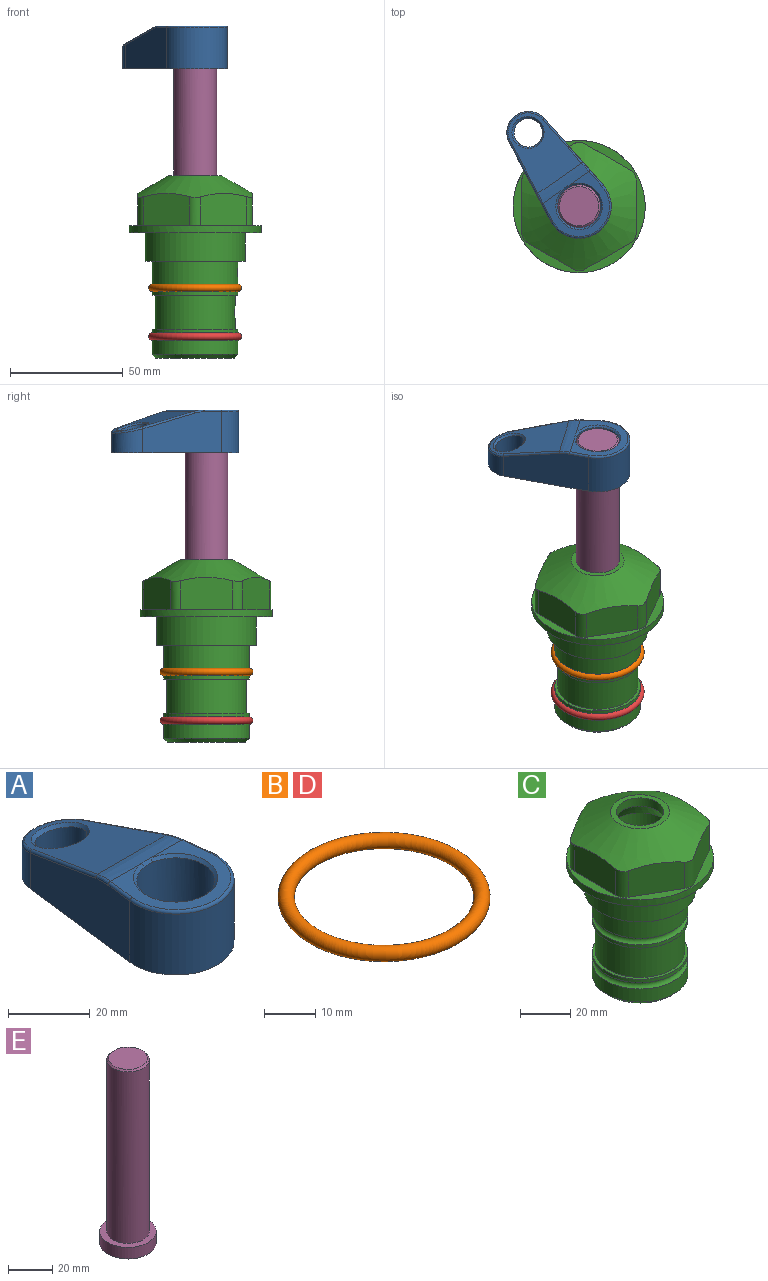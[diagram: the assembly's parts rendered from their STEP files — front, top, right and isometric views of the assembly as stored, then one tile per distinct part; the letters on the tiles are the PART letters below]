
ASSEMBLY  parts=5 mates=4
PART A: 31 faces, bbox 31.7x65.5x19.8 mm
  f0: plane 39.12x18.26mm, normal (0.99,0.12,0), area 612.2mm2, adj f1,f4,f7,f11,f13,f15
  f1: cylinder r=9.53mm len=18.91mm, axis (0,0,-1), area 296.1mm2, adj f0,f2,f7,f17
  f2: plane 39.12x18.26mm, normal (-0.99,0.12,0), area 612.2mm2, adj f1,f4,f7,f12,f14,f16
  f3: cylinder r=6.35mm len=12.7mm, axis (0,0,-1), area 362.4mm2, adj f7,f18
  f4: cylinder r=14.29mm len=28.58mm, axis (0,0,-1), area 882.2mm2, adj f0,f2,f7,f10
  f5: cylinder r=9.53mm len=19.05mm, axis (0,0,-1), area 1092.6mm2, adj f7,f19,f20
  f6: plane 26.99x23.69mm, normal (0,0,1), area 216.2mm2, adj f9,f10,f11,f12,f19
  f7: plane 63.5x28.58mm, normal (0,0,-1), area 661.8mm2, adj f0,f1,f2,f3,f4,f5,f22,f23
  f8: plane 33.52x23.6mm, normal (0,0.26,0.97), area 486mm2, adj f9,f15,f16,f17,f18
  f9: cylinder r=19.05mm len=24.72mm, axis (1,0,0), area 120.4mm2, adj f6,f8,f13,f14,f20
  f10: torus R=13.49mm, axis (0,0,1), area 59mm2, adj f4,f6,f11,f12
  f11: cylinder r=0.79mm len=8.67mm, axis (0.12,-0.99,0), area 10.8mm2, adj f0,f6,f10,f13
  f12: cylinder r=0.79mm len=8.67mm, axis (0.12,0.99,0), area 10.8mm2, adj f2,f6,f10,f14
  f13: bspline ~4.95x1.42mm, area 6.1mm2, adj f0,f9,f11,f15
  f14: bspline ~4.95x1.42mm, area 6.1mm2, adj f2,f9,f12,f16
  f15: cylinder r=0.79mm len=25.95mm, axis (0.12,-0.96,0.26), area 32.9mm2, adj f0,f8,f13,f17
  f16: cylinder r=0.79mm len=25.95mm, axis (0.12,0.96,-0.26), area 32.9mm2, adj f2,f8,f14,f17
  f17: bspline ~18.91x8.38mm, area 30mm2, adj f1,f8,f15,f16
  f18: bspline ~14.29x14.29mm, area 48.3mm2, adj f3,f8
  f19: cone r=9.53mm half-angle=45deg, axis (0,0,1), area 66.5mm2, adj f5,f6,f20
  f20: bspline ~3.22x0.96mm, area 3.5mm2, adj f5,f9,f19
  f21: plane 2.75x2.72mm, normal (0,0,-1), area 2.9mm2, adj f23,f25,f28
  f22: plane 23.05x15.88mm, normal (-0.99,-0.12,0), area 323.6mm2, adj f7,f25,f26,f27,f28,f29
  f23: plane 23.05x15.88mm, normal (0.99,-0.12,0), area 323.6mm2, adj f7,f21,f25,f27,f28,f30
  f24: cylinder r=9.53mm len=10.69mm, axis (0,0,-1), area 114.7mm2, adj f7,f27,f29,f30
  f25: cylinder r=12.7mm len=20.59mm, axis (0,0,-1), area 381.1mm2, adj f7,f21,f22,f23,f26,f28
  f26: plane 2.75x2.72mm, normal (0,0,-1), area 2.9mm2, adj f22,f25,f28
  f27: plane 19.72x18.37mm, normal (0,-0.26,-0.97), area 291.8mm2, adj f22,f23,f24,f28,f29,f30
  f28: cylinder r=15.88mm len=19.92mm, axis (1,0,0), area 54.8mm2, adj f21,f22,f23,f25,f26,f27
  f29: cylinder r=1.59mm len=11mm, axis (0,0,-1), area 34.7mm2, adj f7,f22,f24,f27
  f30: cylinder r=1.59mm len=11mm, axis (0,0,-1), area 34.7mm2, adj f7,f23,f24,f27
PART B: 1 faces, bbox 44.7x44.7x3.2 mm
  f0: torus R=19.05mm, axis (0,0,1), area 1193.9mm2
PART C: 36 faces, bbox 58.7x58.7x81 mm
  f0: cylinder r=17.78mm len=35.56mm, axis (0,0,1), area 1670.8mm2, adj f23,f24,f31
  f1: cylinder r=19.05mm len=38.1mm, axis (0,0,1), area 1191.9mm2, adj f26,f27,f30
  f2: plane 58.66x58.66mm, normal (0,0,-1), area 1150.6mm2, adj f3,f28
  f3: cylinder r=29.33mm len=58.66mm, axis (0,0,-1), area 585.1mm2, adj f2,f4
  f4: plane 58.66x58.66mm, normal (0,0,1), area 475.9mm2, adj f3,f5,f6,f7,f8,f9,f10,f11
  f5: plane 20.32x14.34mm, normal (-0.5,0.87,0), area 324.4mm2, adj f4,f15,f16,f17
  f6: plane 20.32x14.34mm, normal (0.5,0.87,0), area 324.4mm2, adj f4,f14,f15,f17
  f7: plane 23.48x14.34mm, normal (1,0,0), area 324.4mm2, adj f4,f13,f14,f17
  f8: plane 20.32x14.34mm, normal (0.5,-0.87,0), area 324.4mm2, adj f4,f12,f13,f17
  f9: plane 20.32x14.34mm, normal (-0.5,-0.87,0), area 324.4mm2, adj f4,f11,f12,f17
  f10: plane 23.48x14.34mm, normal (-1,0,0), area 324.4mm2, adj f4,f11,f16,f17
  f11: cylinder r=5.08mm len=12.85mm, axis (0,0,-1), area 67.2mm2, adj f4,f9,f10,f17
  f12: cylinder r=5.08mm len=12.85mm, axis (0,0,-1), area 67.2mm2, adj f4,f8,f9,f17
  f13: cylinder r=5.08mm len=12.85mm, axis (0,0,-1), area 67.2mm2, adj f4,f7,f8,f17
  f14: cylinder r=5.08mm len=12.85mm, axis (0,0,-1), area 67.2mm2, adj f4,f6,f7,f17
  f15: cylinder r=5.08mm len=12.85mm, axis (0,0,-1), area 67.2mm2, adj f4,f5,f6,f17
  f16: cylinder r=5.08mm len=12.85mm, axis (0,0,-1), area 67.2mm2, adj f4,f5,f10,f17
  f17: cone r=11.73mm half-angle=60deg, axis (0,0,-1), area 2071.8mm2, adj f5,f6,f7,f8,f9,f10,f11,f12
  f18: plane 23.46x23.46mm, normal (0,0,1), area 147.4mm2, adj f17,f35
  f19: plane 34.93x34.93mm, normal (0,0,-1), area 958mm2, adj f29
  f20: cylinder r=19.05mm len=38.1mm, axis (0,0,1), area 760.1mm2, adj f21,f29
  f21: torus R=19.05mm, axis (0,0,1), area 565.3mm2, adj f20,f22
  f22: cylinder r=19.05mm len=38.1mm, axis (0,0,1), area 190mm2, adj f21,f23
  f23: plane 38.1x38.1mm, normal (0,0,1), area 146.9mm2, adj f0,f22
  f24: plane 38.1x38.1mm, normal (0,0,-1), area 146.9mm2, adj f0,f25
  f25: cylinder r=19.05mm len=38.1mm, axis (0,0,1), area 190mm2, adj f24,f26
  f26: torus R=19.05mm, axis (0,0,1), area 565.3mm2, adj f1,f25
  f27: plane 44.45x44.45mm, normal (0,0,-1), area 411.7mm2, adj f1,f28
  f28: cylinder r=22.23mm len=44.45mm, axis (0,0,1), area 1773.5mm2, adj f2,f27
  f29: cone r=19.05mm half-angle=45deg, axis (0,0,1), area 257.5mm2, adj f19,f20
  f30: cylinder r=3.17mm len=6.75mm, axis (-1,0,0), area 128mm2, adj f1,f33
  f31: cylinder r=3.17mm len=6.35mm, axis (-1,0,0), area 102.5mm2, adj f0,f33
  f32: plane 25.4x25.4mm, normal (0,0,1), area 506.7mm2, adj f33
  f33: cylinder r=12.7mm len=66.42mm, axis (0,0,-1), area 5236.2mm2, adj f30,f31,f32,f34
  f34: cone r=9.53mm half-angle=30deg, axis (0,0,-1), area 443.4mm2, adj f33,f35
  f35: cylinder r=9.53mm len=19.05mm, axis (0,0,-1), area 240.9mm2, adj f18,f34
PART D: same geometry as B
PART E: 6 faces, bbox 25.4x25.4x101.6 mm
  f0: plane 17.46x17.46mm, normal (0,0,1), area 239.5mm2, adj f5
  f1: plane 25.4x25.4mm, normal (0,0,-1), area 506.7mm2, adj f2
  f2: cylinder r=12.7mm len=25.4mm, axis (0,0,1), area 506.7mm2, adj f1,f3
  f3: plane 25.4x25.4mm, normal (0,0,1), area 221.7mm2, adj f2,f4
  f4: cylinder r=9.53mm len=94.46mm, axis (0,0,1), area 5653mm2, adj f3,f5
  f5: cone r=8.73mm half-angle=45deg, axis (0,0,-1), area 64.4mm2, adj f0,f4
PLACE A rot(axis=(0,0,1),34.6deg) t=(0,0,28.35)mm
PLACE B at identity
PLACE C at identity fixed
PLACE D t=(0,0,-21.59)mm
PLACE E rot(axis=(0,0,1),34.6deg) t=(0,0,27.55)mm
MATE fastened D.f0 <-> C.f0  axis (0,0,1) through (0,0,-46.1)mm
MATE cylindrical C.f0 <-> E.f2  axis (0,0,1) through (0,0,-50.55)mm
MATE fastened E.f2 <-> A.f4  axis (0,0,1) through (0,0,91.05)mm
MATE fastened B.f0 <-> C.f0  axis (0,0,1) through (0,0,-24.51)mm
